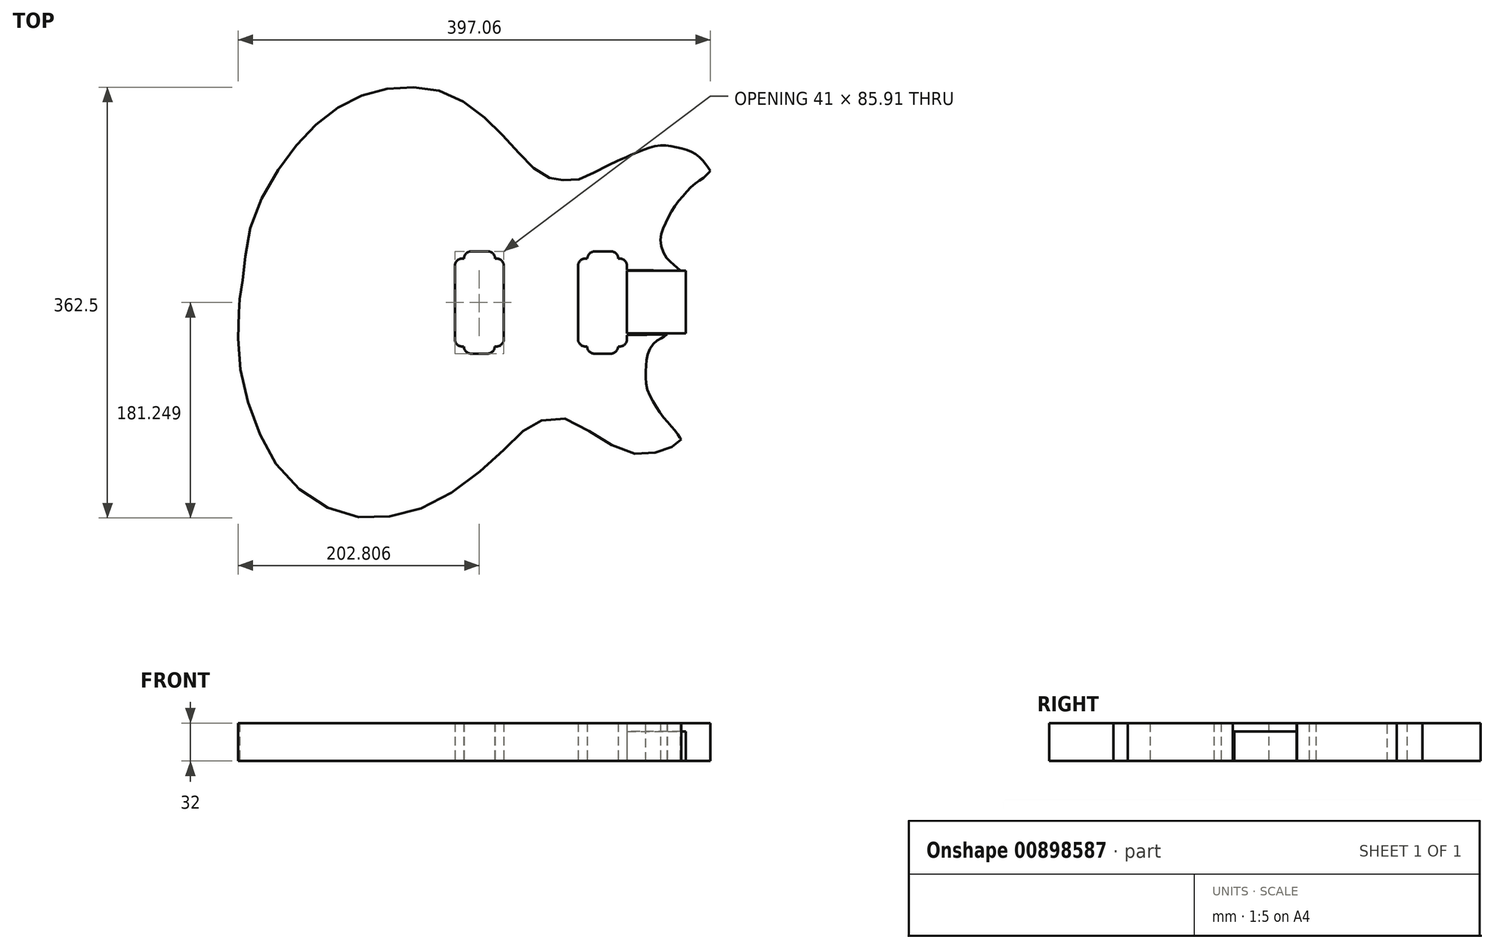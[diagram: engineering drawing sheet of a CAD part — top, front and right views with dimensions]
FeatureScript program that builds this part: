
annotation { "Feature Type Name" : "Feature", "Feature Type Description" : "" }
export const myFeature = defineFeature(function(context is Context, id is Id, definition is map)
    precondition{}
    {
        {
            var Q0;
            Q0=qCreatedBy(makeId("Top.planeOp"),FACE);
            var sketch = newSketch(context, id + "F0", { "sketchPlane" : qUnion([Q0])});
            skLineSegment(sketch, "E0", {"start": v(-187.33, 0.42) * mm, "end": v(-177.33, 0.42) * mm});
            skLineSegment(sketch, "E1", {"start": v(142.67, 0.42) * mm, "end": v(162.67, 0.42) * mm});
            skArc(sketch, "E2", {"start": v(-2.8, 43.38) * mm, "mid": v(-7.05, 41.62) * mm, "end": v(-8.8, 37.38) * mm});
            skLineSegment(sketch, "E3", {"start": v(-8.8, 37.38) * mm, "end": v(-10.48, 37.38) * mm});
            skArc(sketch, "E4", {"start": v(-10.48, 37.38) * mm, "mid": v(-14.73, 35.62) * mm, "end": v(-16.48, 31.38) * mm});
            skLineSegment(sketch, "E5", {"start": v(-16.48, 31.38) * mm, "end": v(-16.48, -30.54) * mm});
            skArc(sketch, "E6", {"start": v(-16.48, -30.54) * mm, "mid": v(-14.73, -34.78) * mm, "end": v(-10.48, -36.54) * mm});
            skLineSegment(sketch, "E7", {"start": v(-10.48, -36.54) * mm, "end": v(-8.98, -36.54) * mm});
            skArc(sketch, "E8", {"start": v(-8.98, -36.54) * mm, "mid": v(-7.23, -40.78) * mm, "end": v(-2.98, -42.54) * mm});
            skLineSegment(sketch, "E9", {"start": v(-2.98, -42.54) * mm, "end": v(11.02, -42.54) * mm});
            skArc(sketch, "E10", {"start": v(11.02, -42.54) * mm, "mid": v(15.26, -40.78) * mm, "end": v(17.02, -36.54) * mm});
            skLineSegment(sketch, "E11", {"start": v(17.02, -36.54) * mm, "end": v(18.52, -36.54) * mm});
            skArc(sketch, "E12", {"start": v(18.52, -36.54) * mm, "mid": v(22.76, -34.78) * mm, "end": v(24.52, -30.54) * mm});
            skLineSegment(sketch, "E13", {"start": v(24.52, -30.54) * mm, "end": v(24.52, 31.38) * mm});
            skArc(sketch, "E14", {"start": v(24.52, 31.38) * mm, "mid": v(22.76, 35.62) * mm, "end": v(18.52, 37.38) * mm});
            skLineSegment(sketch, "E15", {"start": v(18.52, 37.38) * mm, "end": v(17.2, 37.38) * mm});
            skArc(sketch, "E16", {"start": v(17.2, 37.38) * mm, "mid": v(15.44, 41.62) * mm, "end": v(11.2, 43.38) * mm});
            skLineSegment(sketch, "E17", {"start": v(11.2, 43.38) * mm, "end": v(-2.8, 43.38) * mm});
            skLineSegment(sketch, "E18", {"start": v(128.12, -30.54) * mm, "end": v(128.12, -17.58) * mm});
            skLineSegment(sketch, "E19", {"start": v(142.67, 0.42) * mm, "end": v(172.67, 0.42) * mm});
            skLineSegment(sketch, "E20", {"start": v(177.65, -26.3) * mm, "end": v(128.12, -27) * mm});
            skLineSegment(sketch, "E21", {"start": v(177.65, 27.14) * mm, "end": v(128.12, 27.84) * mm});
            skArc(sketch, "E22", {"start": v(100.8, 43.38) * mm, "mid": v(96.55, 41.62) * mm, "end": v(94.8, 37.38) * mm});
            skLineSegment(sketch, "E23", {"start": v(94.8, 37.38) * mm, "end": v(93.12, 37.38) * mm});
            skArc(sketch, "E24", {"start": v(93.12, 37.38) * mm, "mid": v(88.88, 35.62) * mm, "end": v(87.12, 31.38) * mm});
            skLineSegment(sketch, "E25", {"start": v(87.12, 31.38) * mm, "end": v(87.12, -30.54) * mm});
            skArc(sketch, "E26", {"start": v(87.12, -30.54) * mm, "mid": v(88.88, -34.78) * mm, "end": v(93.12, -36.54) * mm});
            skLineSegment(sketch, "E27", {"start": v(93.12, -36.54) * mm, "end": v(94.62, -36.54) * mm});
            skArc(sketch, "E28", {"start": v(94.62, -36.54) * mm, "mid": v(96.38, -40.78) * mm, "end": v(100.62, -42.54) * mm});
            skLineSegment(sketch, "E29", {"start": v(100.62, -42.54) * mm, "end": v(114.62, -42.54) * mm});
            skArc(sketch, "E30", {"start": v(114.62, -42.54) * mm, "mid": v(118.86, -40.78) * mm, "end": v(120.62, -36.54) * mm});
            skLineSegment(sketch, "E31", {"start": v(120.62, -36.54) * mm, "end": v(122.12, -36.54) * mm});
            skArc(sketch, "E32", {"start": v(122.12, -36.54) * mm, "mid": v(126.36, -34.78) * mm, "end": v(128.12, -30.54) * mm});
            skLineSegment(sketch, "E33", {"start": v(128.12, -30.54) * mm, "end": v(128.12, 31.38) * mm});
            skArc(sketch, "E34", {"start": v(128.12, 31.38) * mm, "mid": v(126.36, 35.62) * mm, "end": v(122.12, 37.38) * mm});
            skLineSegment(sketch, "E35", {"start": v(122.12, 37.38) * mm, "end": v(120.8, 37.38) * mm});
            skArc(sketch, "E36", {"start": v(120.8, 37.38) * mm, "mid": v(119.04, 41.62) * mm, "end": v(114.8, 43.38) * mm});
            skLineSegment(sketch, "E37", {"start": v(114.8, 43.38) * mm, "end": v(100.8, 43.38) * mm});
            skArc(sketch, "E38", {"start": v(94.8, 37.38) * mm, "mid": v(96.55, 33.13) * mm, "end": v(100.8, 31.38) * mm});
            skLineSegment(sketch, "E39", {"start": v(100.8, 31.38) * mm, "end": v(114.8, 31.38) * mm});
            skArc(sketch, "E40", {"start": v(114.8, 31.38) * mm, "mid": v(119.04, 33.13) * mm, "end": v(120.8, 37.38) * mm});
            skArc(sketch, "E41", {"start": v(100.62, -30.54) * mm, "mid": v(96.38, -32.3) * mm, "end": v(94.62, -36.54) * mm});
            skArc(sketch, "E42", {"start": v(120.62, -36.54) * mm, "mid": v(118.86, -32.3) * mm, "end": v(114.62, -30.54) * mm});
            skLineSegment(sketch, "E43", {"start": v(114.62, -30.54) * mm, "end": v(100.62, -30.54) * mm});
            skLineSegment(sketch, "E44", {"start": v(177.65, 27.14) * mm, "end": v(177.65, -26.3) * mm});
            skLineSegment(sketch, "E45", {"start": v(87.12, 28.42) * mm, "end": v(87.12, -27.57) * mm});
            skLineSegment(sketch, "E46", {"start": v(177.65, 27.14) * mm, "end": v(177.65, -25.35) * mm});
            skLineSegment(sketch, "E47", {"start": v(177.65, -25.35) * mm, "end": v(128.12, -25.35) * mm});
            skLineSegment(sketch, "E48", {"start": v(128.12, -25.35) * mm, "end": v(128.12, 27.14) * mm});
            skLineSegment(sketch, "E49", {"start": v(128.12, 27.14) * mm, "end": v(177.65, 27.14) * mm});
            skFitSpline(sketch, "E50", {"points": [v(172.67, 27.42) * mm, v(167.87, 32) * mm, v(160.88, 38.66) * mm, v(156.14, 53.28) * mm, v(160.2, 66.02) * mm, v(167.17, 79.76) * mm, v(176.39, 91.56) * mm, v(185.68, 100.84) * mm, v(193.5, 106.22) * mm, v(196.79, 109.65) * mm, v(198.27, 111.2) * mm]});
            skFitSpline(sketch, "E51", {"points": [v(198.27, 111.2) * mm, v(196.74, 113.29) * mm, v(192.73, 118.74) * mm, v(184.27, 126.33) * mm, v(171.23, 130.86) * mm, v(156.33, 132.56) * mm, v(141.23, 128.65) * mm, v(129.59, 123.81) * mm, v(122.98, 120.84) * mm, v(120.85, 119.88) * mm]});
            skFitSpline(sketch, "E52", {"points": [v(-197.32, 3.57) * mm, v(-194.15, 24.72) * mm, v(-188.1, 65.1) * mm, v(-162.02, 116.35) * mm, v(-130.86, 152.3) * mm, v(-96.72, 173.76) * mm, v(-59.75, 181.55) * mm, v(-22.56, 176.18) * mm, v(9.42, 155.06) * mm, v(33.5, 130.56) * mm, v(51.26, 112.14) * mm, v(66.29, 104.09) * mm, v(76.6, 103.32) * mm, v(90.89, 104.78) * mm, v(104.66, 112.22) * mm, v(115.41, 117.31) * mm, v(120.85, 119.88) * mm]});
            skFitSpline(sketch, "E53", {"points": [v(-197.32, 3.57) * mm, v(-197.62, -0.64) * mm, v(-198.3, -9.82) * mm, v(-198.65, -34.47) * mm, v(-194.49, -67.58) * mm, v(-182.7, -104.97) * mm, v(-164.68, -138.12) * mm, v(-136.17, -164.98) * mm, v(-102.76, -179.37) * mm, v(-71, -179.45) * mm, v(-37.05, -169.3) * mm, v(-2.5, -147.27) * mm, v(24.47, -123.74) * mm, v(41.29, -107.2) * mm, v(54.14, -99.79) * mm, v(72.06, -96.35) * mm, v(93.65, -105.94) * mm, v(113.75, -118.64) * mm, v(132.94, -126.6) * mm, v(147.57, -126.1) * mm, v(159.3, -124.58) * mm, v(167.7, -119.63) * mm, v(171.92, -116.17) * mm, v(173.67, -114.73) * mm]});
            skFitSpline(sketch, "E54", {"points": [v(161.8, -26.58) * mm, v(158.37, -28.73) * mm, v(151.62, -33) * mm, v(145.43, -43.87) * mm, v(144.02, -55.9) * mm, v(144.52, -69.93) * mm, v(150.74, -84.17) * mm, v(159.64, -97.3) * mm, v(168.1, -106.7) * mm, v(172.2, -112.62) * mm, v(173.67, -114.73) * mm]});
            skLineSegment(sketch, "E55", {"start": v(172.67, 27.42) * mm, "end": v(172.91, 27.2) * mm});
            skLineSegment(sketch, "E56", {"start": v(161.8, -26.58) * mm, "end": v(161.89, -26.52) * mm});
            skSolve(sketch);
        }
        {
            var Q0;
            Q0=makeQuery(id+"F0.imprint","IMPRINT",FACE,{"disambiguationData":[TD([[makeQuery(id+"F0.imprint","IMPRINT",EDGE,{"derivedFrom":sQuery(id+"F0.wireOp",EDGE,"E2")}),-1.0]])]});
            extrude(context, id + "F1", {"entities" : qUnion([Q0]), "depth" : 32 * mm, "offsetDistance" : 25 * mm});
        }
        {
            var Q0;
            {var subQ2=sQuery(id+"F0.wireOp",EDGE,"E47");Q0=makeQuery(id+"F0.imprint","IMPRINT",FACE,{"disambiguationData":[TD([[makeQuery(id+"F0.imprint","IMPRINT",EDGE,{"derivedFrom":subQ2}),-1.0]])]});}
            extrude(context, id + "F2", {"entities" : qUnion([Q0]), "operationType" : NewBodyOperationType.ADD, "depth" : 25 * mm, "offsetDistance" : 25 * mm});
        }
    });
